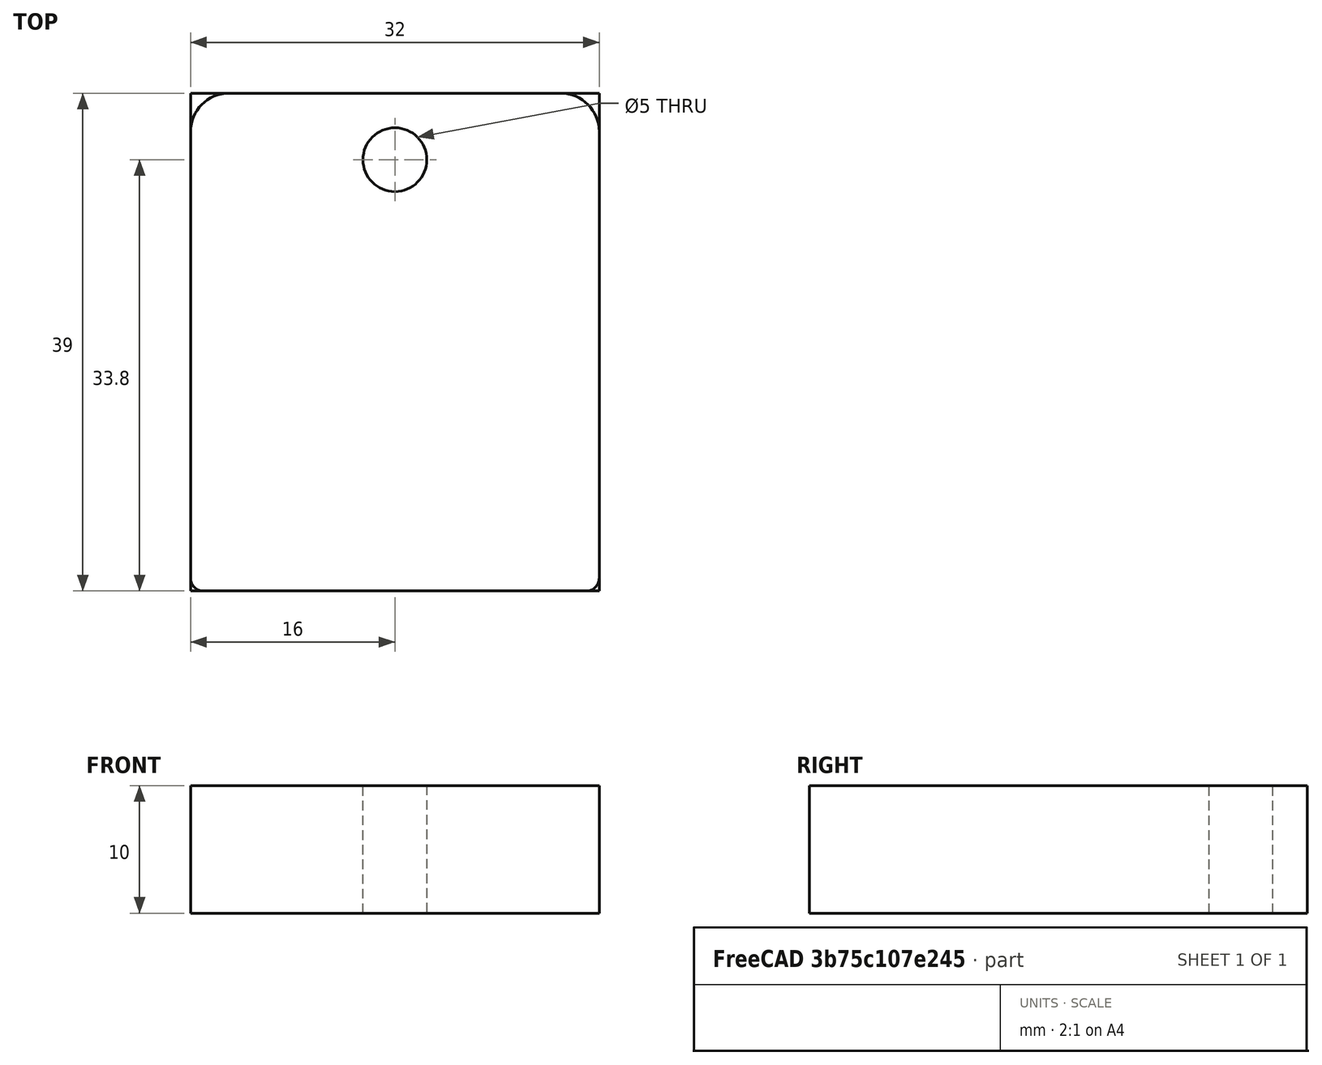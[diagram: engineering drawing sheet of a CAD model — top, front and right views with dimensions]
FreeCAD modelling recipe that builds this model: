
FCSTD DOCUMENT  (FreeCAD 0.16R)
Label: BabyGateSpacer
License: All rights reserved
LicenseURL: http://en.wikipedia.org/wiki/All_rights_reserved
objects: Sketcher::SketchObject×2, PartDesign::Fillet×2, PartDesign::Pad×1, PartDesign::Pocket×1, Mesh::Feature×1
note: 8 computed .brp shape members not serialized (recipe doc carries the construction recipe); baked Part::Feature solids carry a one-line shape summary decoded from their .brp

FEATURE [Sketcher::SketchObject] Sketch
  sketch-geometry (4):
    g0: LineSegment StartX=-16 StartY=19.5 StartZ=0 EndX=16 EndY=19.5 EndZ=0
    g1: LineSegment StartX=16 StartY=19.5 StartZ=0 EndX=16 EndY=-19.5 EndZ=0
    g2: LineSegment StartX=16 StartY=-19.5 StartZ=0 EndX=-16 EndY=-19.5 EndZ=0
    g3: LineSegment StartX=-16 StartY=-19.5 StartZ=0 EndX=-16 EndY=19.5 EndZ=0
  constraints (11):
    c: Coincident(g0,g1)
    c: Coincident(g1,g2)
    c: Coincident(g2,g3)
    c: Coincident(g3,g0)
    c: Horizontal(g0)
    c: Horizontal(g2)
    c: Vertical(g1)
    c: Vertical(g3)
    c: Symmetric(g2,g0,g-1)
    c: Distance(g0) = 32
    c: Distance(g1) = 39
FEATURE [PartDesign::Pad] Pad
  Length = 10
  Length2 = 100
  Sketch = -> Sketch
  Type = 0
FEATURE [Sketcher::SketchObject] Sketch001
  ExternalGeometry = -> [Pad]
  Placement = pos=(0,0,10) rot=(0,0,1;0rad)
  Support = -> Pad [Face6]
  sketch-geometry (1):
    g0: Circle CenterX=0 CenterY=14.3 CenterZ=0 NormalX=0 NormalY=0 NormalZ=1 Radius=2.5
  constraints (3):
    c: Radius(g0) = 2.5
    c: PointOnObject(g0,g-2)
    c: Distance(g0,g-3) = 5.2
FEATURE [PartDesign::Pocket] Pocket
  Length = 5
  Sketch = -> Sketch001
  Type = 1
FEATURE [PartDesign::Fillet] Fillet
  Base = -> Pocket [Edge1,Edge2]
  Radius = 3
FEATURE [PartDesign::Fillet] Fillet001
  Base = -> Fillet [Edge19,Edge20]
  Radius = 1
FEATURE [Mesh::Feature] Mesh  label="Fillet001 (Meshed)"
